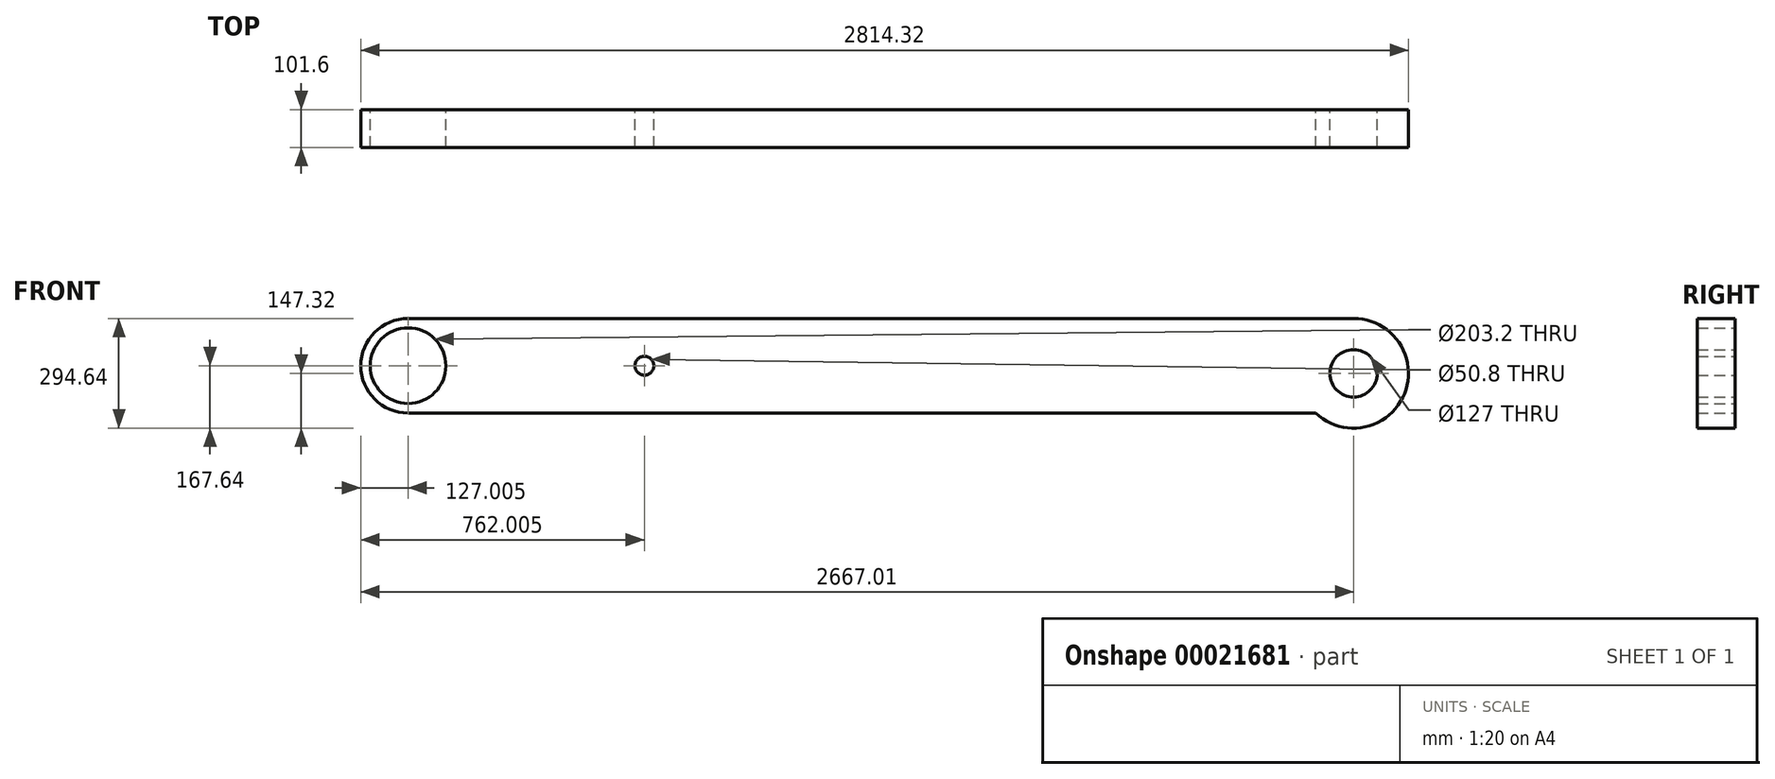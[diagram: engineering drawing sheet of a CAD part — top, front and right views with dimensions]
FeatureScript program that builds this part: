
annotation { "Feature Type Name" : "Feature", "Feature Type Description" : "" }
export const myFeature = defineFeature(function(context is Context, id is Id, definition is map)
    precondition{}
    {
        {
            var Q0;
            Q0=qCreatedBy(makeId("Front.planeOp"),FACE);
            var sketch = newSketch(context, id + "F0", { "sketchPlane" : qUnion([Q0])});
            skLineSegment(sketch, "E0", {"start": v(-990.98, 254) * mm, "end": v(1549.02, 254) * mm});
            skArc(sketch, "E1", {"start": v(1447.42, 0) * mm, "mid": v(1685.8, 51.97) * mm, "end": v(1549.02, 254) * mm});
            skArc(sketch, "E2", {"start": v(-990.98, 254) * mm, "mid": v(-1117.98, 127) * mm, "end": v(-990.98, 0) * mm});
            skLineSegment(sketch, "E3", {"start": v(-990.98, 0) * mm, "end": v(1447.42, 0) * mm});
            skCircle(sketch, "E4", {"center": v(-355.98, 127) * mm, "radius": 25.4 * mm});
            skCircle(sketch, "E5", {"center": v(-990.98, 127) * mm, "radius": 101.6 * mm});
            skCircle(sketch, "E6", {"center": v(1549.02, 106.68) * mm, "radius": 63.5 * mm});
            skSolve(sketch);
        }
        {
            var Q0;
            Q0=makeQuery(id+"F0.imprint","IMPRINT",FACE,{"disambiguationData":[TD([[makeQuery(id+"F0.imprint","IMPRINT",EDGE,{"derivedFrom":sQuery(id+"F0.wireOp",EDGE,"E0")}),-1.0]])]});
            extrude(context, id + "F1", {"entities" : qUnion([Q0]), "depth" : 101.6 * mm});
        }
    });
